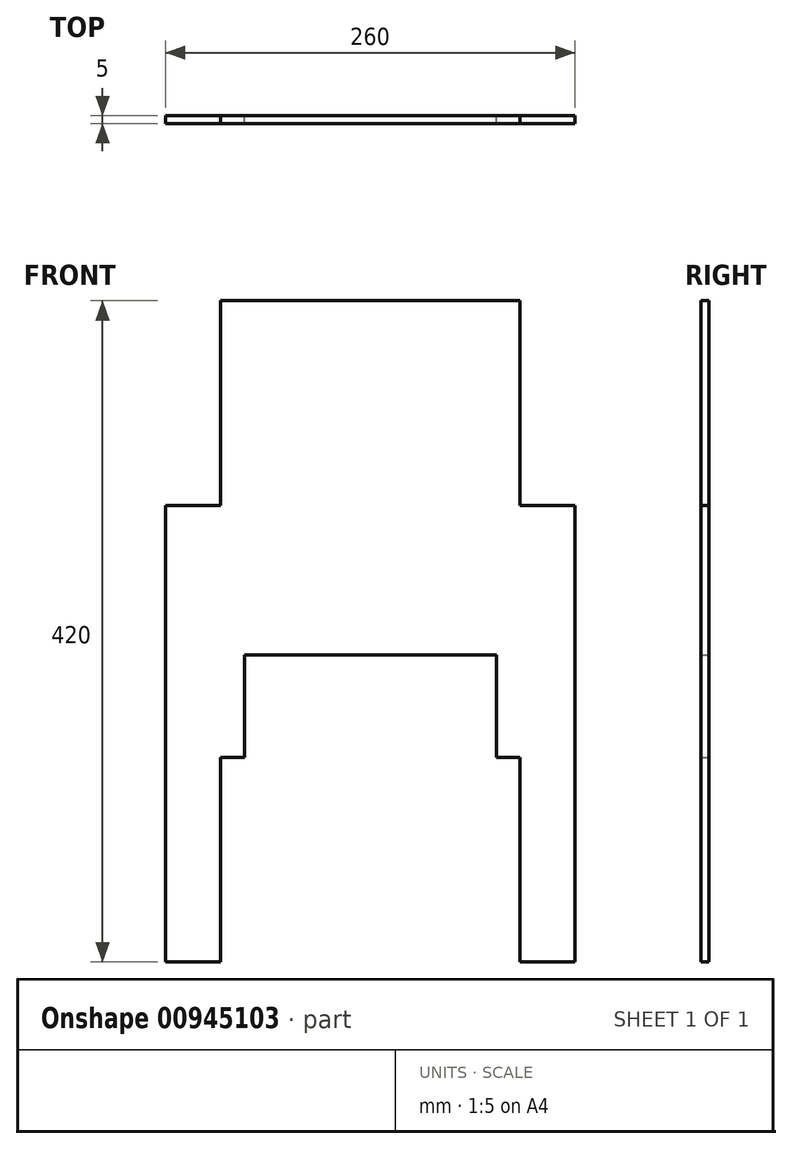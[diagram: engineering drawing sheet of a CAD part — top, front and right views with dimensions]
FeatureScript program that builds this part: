
annotation { "Feature Type Name" : "Feature", "Feature Type Description" : "" }
export const myFeature = defineFeature(function(context is Context, id is Id, definition is map)
    precondition{}
    {
        {
            var Q0;
            Q0=qCreatedBy(makeId("Front.planeOp"),FACE);
            var sketch = newSketch(context, id + "F0", { "sketchPlane" : qUnion([Q0])});
            skLineSegment(sketch, "E0", {"start": v(-42.94, -139.52) * mm, "end": v(-42.94, 150.48) * mm});
            skLineSegment(sketch, "E1", {"start": v(-42.94, 150.48) * mm, "end": v(-7.94, 150.48) * mm});
            skLineSegment(sketch, "E2", {"start": v(217.06, 150.48) * mm, "end": v(217.06, -139.52) * mm});
            skLineSegment(sketch, "E3", {"start": v(-42.94, -139.52) * mm, "end": v(-7.94, -139.52) * mm});
            skLineSegment(sketch, "E4", {"start": v(-7.94, -139.52) * mm, "end": v(-7.94, -9.52) * mm});
            skLineSegment(sketch, "E5", {"start": v(-7.94, -9.52) * mm, "end": v(7.06, -9.52) * mm});
            skLineSegment(sketch, "E6", {"start": v(7.06, -9.52) * mm, "end": v(7.06, 55.48) * mm});
            skLineSegment(sketch, "E7", {"start": v(7.06, 55.48) * mm, "end": v(167.06, 55.48) * mm});
            skLineSegment(sketch, "E8", {"start": v(167.06, 55.48) * mm, "end": v(167.06, -9.52) * mm});
            skLineSegment(sketch, "E9", {"start": v(167.06, -9.52) * mm, "end": v(182.06, -9.52) * mm});
            skLineSegment(sketch, "E10", {"start": v(182.06, -9.52) * mm, "end": v(182.06, -139.52) * mm});
            skLineSegment(sketch, "E11", {"start": v(182.06, -139.52) * mm, "end": v(217.06, -139.52) * mm});
            skLineSegment(sketch, "E12.bottom", {"start": v(-7.94, 280.48) * mm, "end": v(182.06, 280.48) * mm});
            skLineSegment(sketch, "E12.left", {"start": v(-7.94, 280.48) * mm, "end": v(-7.94, 150.48) * mm});
            skLineSegment(sketch, "E12.right", {"start": v(182.06, 280.48) * mm, "end": v(182.06, 150.48) * mm});
            skLineSegment(sketch, "E13.trimOffspring", {"start": v(182.06, 150.48) * mm, "end": v(217.06, 150.48) * mm});
            skSolve(sketch);
        }
        {
            var Q0;
            Q0=makeQuery(id+"F0.imprint","IMPRINT",FACE,{"disambiguationData":[TD([[makeQuery(id+"F0.imprint","IMPRINT",EDGE,{"derivedFrom":sQuery(id+"F0.wireOp",EDGE,"E0")}),-1.0]])]});
            extrude(context, id + "F1", {"entities" : qUnion([Q0]), "depth" : 5 * mm, "offsetDistance" : 25 * mm});
        }
    });
